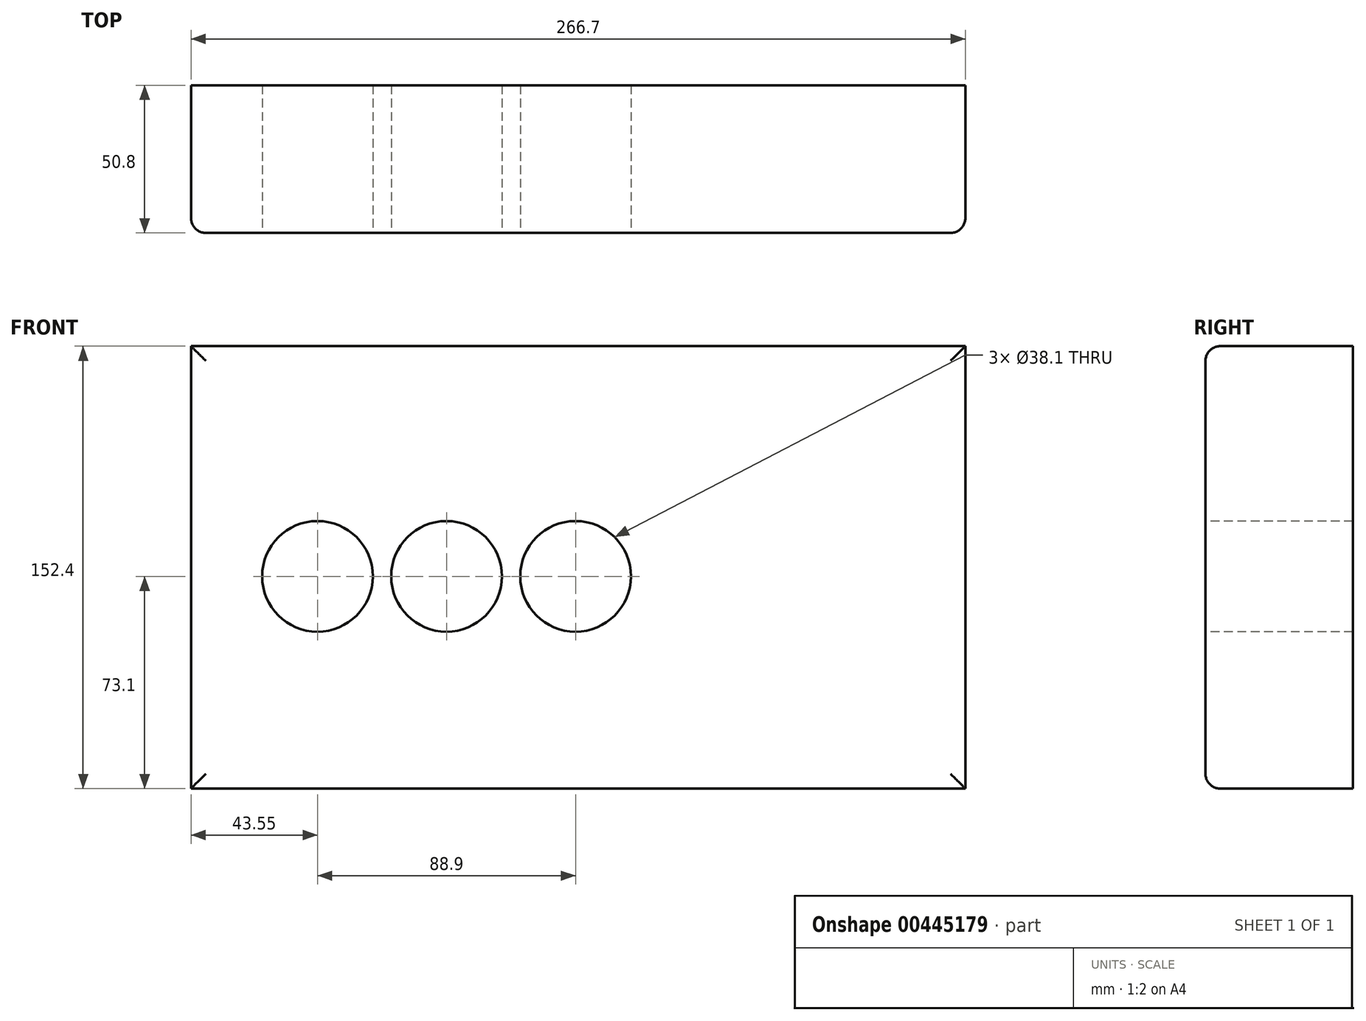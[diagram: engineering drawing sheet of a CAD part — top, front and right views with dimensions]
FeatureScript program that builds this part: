
annotation { "Feature Type Name" : "Feature", "Feature Type Description" : "" }
export const myFeature = defineFeature(function(context is Context, id is Id, definition is map)
    precondition{}
    {
        {
            var Q0;
            Q0=qCreatedBy(makeId("Front.planeOp"),FACE);
            var sketch = newSketch(context, id + "F0", { "sketchPlane" : qUnion([Q0])});
            skLineSegment(sketch, "E0.bottom", {"start": v(178.7, 79.3) * mm, "end": v(-88, 79.3) * mm});
            skLineSegment(sketch, "E0.top", {"start": v(178.7, -73.1) * mm, "end": v(-88, -73.1) * mm});
            skLineSegment(sketch, "E0.left", {"start": v(178.7, 79.3) * mm, "end": v(178.7, -73.1) * mm});
            skLineSegment(sketch, "E0.right", {"start": v(-88, 79.3) * mm, "end": v(-88, -73.1) * mm});
            skSolve(sketch);
        }
        {
            var Q0;
            Q0=makeQuery(id+"F0.imprint","IMPRINT",FACE,{"disambiguationData":[TD([[makeQuery(id+"F0.imprint","IMPRINT",EDGE,{"derivedFrom":sQuery(id+"F0.wireOp",EDGE,"E0.bottom")}),1.0]])]});
            extrude(context, id + "F1", {"entities" : qUnion([Q0]), "depth" : 50.8 * mm});
        }
        {
            var Q0;
            Q0=makeQuery(id+"F1.opExtrude","CAP_FACE",FACE,{"disambiguationData":[OSD([sQuery(id+"F0.wireOp",EDGE,"E0.bottom"),sQuery(id+"F0.wireOp",EDGE,"E0.top"),sQuery(id+"F0.wireOp",EDGE,"E0.left"),sQuery(id+"F0.wireOp",EDGE,"E0.right")])],"isStart":false});
            var sketch = newSketch(context, id + "F2", { "sketchPlane" : qUnion([Q0])});
            skCircle(sketch, "E1", {"center": v(0, 0) * mm, "radius": 19.05 * mm});
            skLineSegment(sketch, "E2", {"start": v(19.05, 0) * mm, "end": v(44.45, 0) * mm});
            skCircle(sketch, "E3", {"center": v(44.45, 0) * mm, "radius": 19.05 * mm});
            skLineSegment(sketch, "E4", {"start": v(-19.05, 0) * mm, "end": v(-44.45, 0) * mm});
            skCircle(sketch, "E5", {"center": v(-44.45, 0) * mm, "radius": 19.05 * mm});
            skSolve(sketch);
        }
        {
            var Q0;
            Q0 = qSketchRegion(id + "F2", true);
            extrude(context, id + "F3", {"entities" : qUnion([Q0]), "operationType" : NewBodyOperationType.REMOVE, "oppositeDirection" : true, "depth" : 50.8 * mm});
        }
        {
            var Q0;
            Q0=makeQuery(id+"F1.opExtrude","CAP_EDGE",EDGE,{"disambiguationData":[OSD([sQuery(id+"F0.wireOp",EDGE,"E0.bottom")])],"isStart":false});
            var Q1;
            Q1=makeQuery(id+"F1.opExtrude","CAP_EDGE",EDGE,{"disambiguationData":[OSD([sQuery(id+"F0.wireOp",EDGE,"E0.right")])],"isStart":false});
            var Q2;
            Q2=makeQuery(id+"F1.opExtrude","CAP_EDGE",EDGE,{"disambiguationData":[OSD([sQuery(id+"F0.wireOp",EDGE,"E0.top")])],"isStart":false});
            var Q3;
            Q3=makeQuery(id+"F1.opExtrude","CAP_EDGE",EDGE,{"disambiguationData":[OSD([sQuery(id+"F0.wireOp",EDGE,"E0.left")])],"isStart":false});
            fillet(context, id + "F4", {"entities" : qUnion([Q0, Q1, Q2, Q3]), "radius" : 5.08 * mm, "tangentPropagation" : true, "allowEdgeOverflow" : false});
        }
    });
